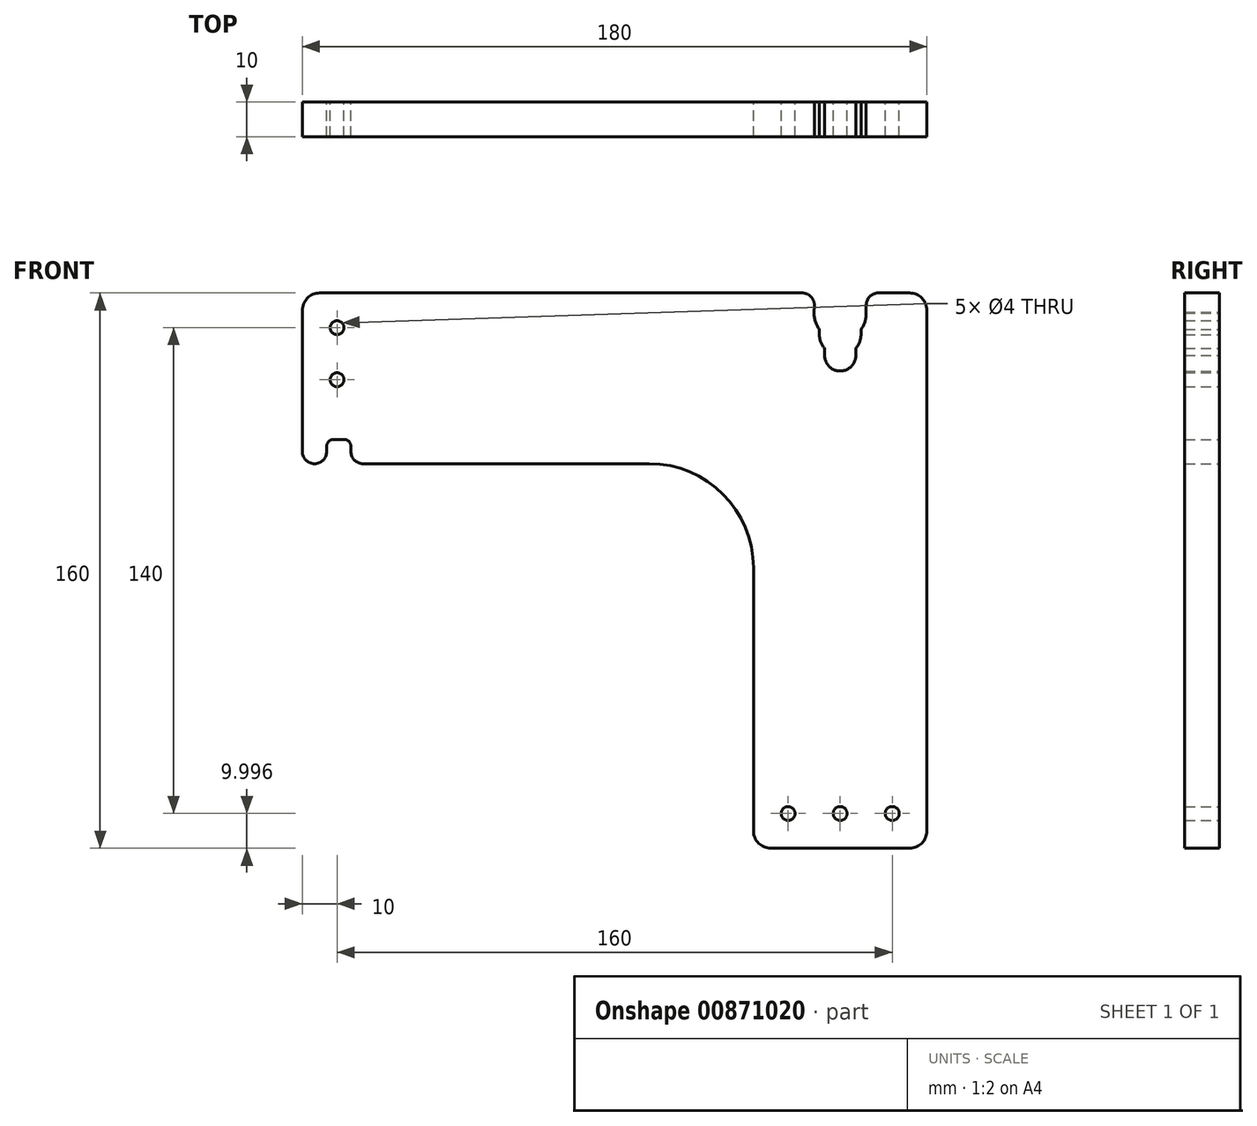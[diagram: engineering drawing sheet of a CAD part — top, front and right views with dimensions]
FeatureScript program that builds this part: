
annotation { "Feature Type Name" : "Feature", "Feature Type Description" : "" }
export const myFeature = defineFeature(function(context is Context, id is Id, definition is map)
    precondition{}
    {
        {
            var Q0;
            Q0=qCreatedBy(makeId("Front.planeOp"),FACE);
            var sketch = newSketch(context, id + "F0", { "sketchPlane" : qUnion([Q0])});
            skCircle(sketch, "E0", {"center": v(0, 0) * mm, "radius": 97.5 * mm, "construction": true});
            skLineSegment(sketch, "E1.bottom", {"start": v(-137.5, -33.5) * mm, "end": v(-55, -33.5) * mm});
            skLineSegment(sketch, "E1.left", {"start": v(-155, -30) * mm, "end": v(-155, 10.7) * mm});
            skLineSegment(sketch, "E2.top", {"start": v(20, -144.3) * mm, "end": v(-20, -144.3) * mm});
            skLineSegment(sketch, "E2.right", {"start": v(-25, -63.5) * mm, "end": v(-25, -139.3) * mm});
            skLineSegment(sketch, "E3", {"start": v(-150, 15.7) * mm, "end": v(-10.94, 15.7) * mm});
            skLineSegment(sketch, "E4", {"start": v(25, 10.7) * mm, "end": v(25, -139.3) * mm});
            skArc(sketch, "E5", {"start": v(-4.5, -2.26) * mm, "mid": v(0, -6.8) * mm, "end": v(4.5, -2.27) * mm});
            skLineSegment(sketch, "E6.trimOffspring", {"start": v(11, 15.7) * mm, "end": v(20, 15.7) * mm});
            skPoint(sketch, "E7.visualSharp", {"position": v(1.31, 15.7) * mm});
            skPoint(sketch, "E8.visualSharp", {"position": v(-1.31, 15.7) * mm});
            skPoint(sketch, "E9.visualSharp", {"position": v(25, 15.7) * mm});
            skArc(sketch, "E9.filletArc", {"start": v(25, 10.7) * mm, "mid": v(23.54, 14.23) * mm, "end": v(20, 15.7) * mm});
            skPoint(sketch, "E10.visualSharp", {"position": v(-25, -33.5) * mm});
            skArc(sketch, "E10.filletArc", {"start": v(-25, -63.5) * mm, "mid": v(-33.79, -42.29) * mm, "end": v(-55, -33.5) * mm});
            skPoint(sketch, "E11.visualSharp", {"position": v(-155, 15.7) * mm});
            skArc(sketch, "E11.filletArc", {"start": v(-150, 15.7) * mm, "mid": v(-153.54, 14.23) * mm, "end": v(-155, 10.7) * mm});
            skPoint(sketch, "E12.visualSharp", {"position": v(-25, -144.3) * mm});
            skArc(sketch, "E12.filletArc", {"start": v(-25, -139.3) * mm, "mid": v(-23.54, -142.84) * mm, "end": v(-20, -144.3) * mm});
            skPoint(sketch, "E13.visualSharp", {"position": v(25, -144.3) * mm});
            skArc(sketch, "E13.filletArc", {"start": v(20, -144.3) * mm, "mid": v(23.54, -142.84) * mm, "end": v(25, -139.3) * mm});
            skCircle(sketch, "E14", {"center": v(-145, -9.3) * mm, "radius": 2 * mm});
            skCircle(sketch, "E15", {"center": v(-145, 5.7) * mm, "radius": 2 * mm});
            skCircle(sketch, "E16", {"center": v(0, -134.3) * mm, "radius": 2 * mm});
            skCircle(sketch, "E17", {"center": v(15, -134.3) * mm, "radius": 2 * mm});
            skCircle(sketch, "E18", {"center": v(-15, -134.3) * mm, "radius": 2 * mm});
            skLineSegment(sketch, "E19", {"start": v(-151.5, -33.5) * mm, "end": v(-151.5, -33.5) * mm});
            skLineSegment(sketch, "E20", {"start": v(-148, -30) * mm, "end": v(-148, -28.5) * mm});
            skLineSegment(sketch, "E21", {"start": v(-146, -26.5) * mm, "end": v(-143, -26.5) * mm});
            skLineSegment(sketch, "E22", {"start": v(-141, -28.5) * mm, "end": v(-141, -30) * mm});
            skPoint(sketch, "E23.visualSharp", {"position": v(-155, -33.5) * mm});
            skArc(sketch, "E23.filletArc", {"start": v(-155, -30) * mm, "mid": v(-153.97, -32.47) * mm, "end": v(-151.5, -33.5) * mm});
            skPoint(sketch, "E24.visualSharp", {"position": v(-148, -33.5) * mm});
            skArc(sketch, "E24.filletArc", {"start": v(-151.5, -33.5) * mm, "mid": v(-149.03, -32.47) * mm, "end": v(-148, -30) * mm});
            skPoint(sketch, "E25.visualSharp", {"position": v(-148, -26.5) * mm});
            skArc(sketch, "E25.filletArc", {"start": v(-146, -26.5) * mm, "mid": v(-147.41, -27.09) * mm, "end": v(-148, -28.5) * mm});
            skPoint(sketch, "E26.visualSharp", {"position": v(-141, -26.5) * mm});
            skArc(sketch, "E26.filletArc", {"start": v(-141, -28.5) * mm, "mid": v(-141.59, -27.09) * mm, "end": v(-143, -26.5) * mm});
            skPoint(sketch, "E27.visualSharp", {"position": v(-141, -33.5) * mm});
            skArc(sketch, "E27.filletArc", {"start": v(-141, -30) * mm, "mid": v(-139.97, -32.47) * mm, "end": v(-137.5, -33.5) * mm});
            skArc(sketch, "E28", {"start": v(-7.49, 10.1) * mm, "mid": v(-7.18, 7.52) * mm, "end": v(-6, 5.2) * mm});
            skArc(sketch, "E29", {"start": v(-6, 3.72) * mm, "mid": v(-5.62, 1.58) * mm, "end": v(-4.5, -0.27) * mm});
            skLineSegment(sketch, "E30", {"start": v(-7.49, 10.1) * mm, "end": v(-7.44, 12.11) * mm});
            skLineSegment(sketch, "E31", {"start": v(7.5, 9.94) * mm, "end": v(7.5, 12.2) * mm});
            skLineSegment(sketch, "E32", {"start": v(6, 3.7) * mm, "end": v(6, 5.2) * mm});
            skLineSegment(sketch, "E33", {"start": v(-6, 3.72) * mm, "end": v(-6, 5.2) * mm});
            skLineSegment(sketch, "E34", {"start": v(-4.5, -2.26) * mm, "end": v(-4.5, -0.27) * mm});
            skLineSegment(sketch, "E35", {"start": v(4.5, -2.27) * mm, "end": v(4.5, -0.27) * mm});
            skArc(sketch, "E36.trimOffspring", {"start": v(6, 5.2) * mm, "mid": v(7.15, 7.44) * mm, "end": v(7.5, 9.94) * mm});
            skArc(sketch, "E37.trimOffspring", {"start": v(4.5, -0.27) * mm, "mid": v(5.61, 1.58) * mm, "end": v(6, 3.7) * mm});
            skPoint(sketch, "E38.visualSharp", {"position": v(-7.36, 15.7) * mm});
            skArc(sketch, "E38.filletArc", {"start": v(-7.44, 12.11) * mm, "mid": v(-8.44, 14.64) * mm, "end": v(-10.94, 15.7) * mm});
            skPoint(sketch, "E39.visualSharp", {"position": v(7.5, 15.7) * mm});
            skArc(sketch, "E39.filletArc", {"start": v(11, 15.7) * mm, "mid": v(8.52, 14.67) * mm, "end": v(7.5, 12.2) * mm});
            skSolve(sketch);
        }
        {
            var Q0;
            Q0 = qSketchRegion(id + "F0", true);
            extrude(context, id + "F1", {"entities" : qUnion([Q0]), "depth" : 10 * mm, "offsetDistance" : 25 * mm});
        }
    });
